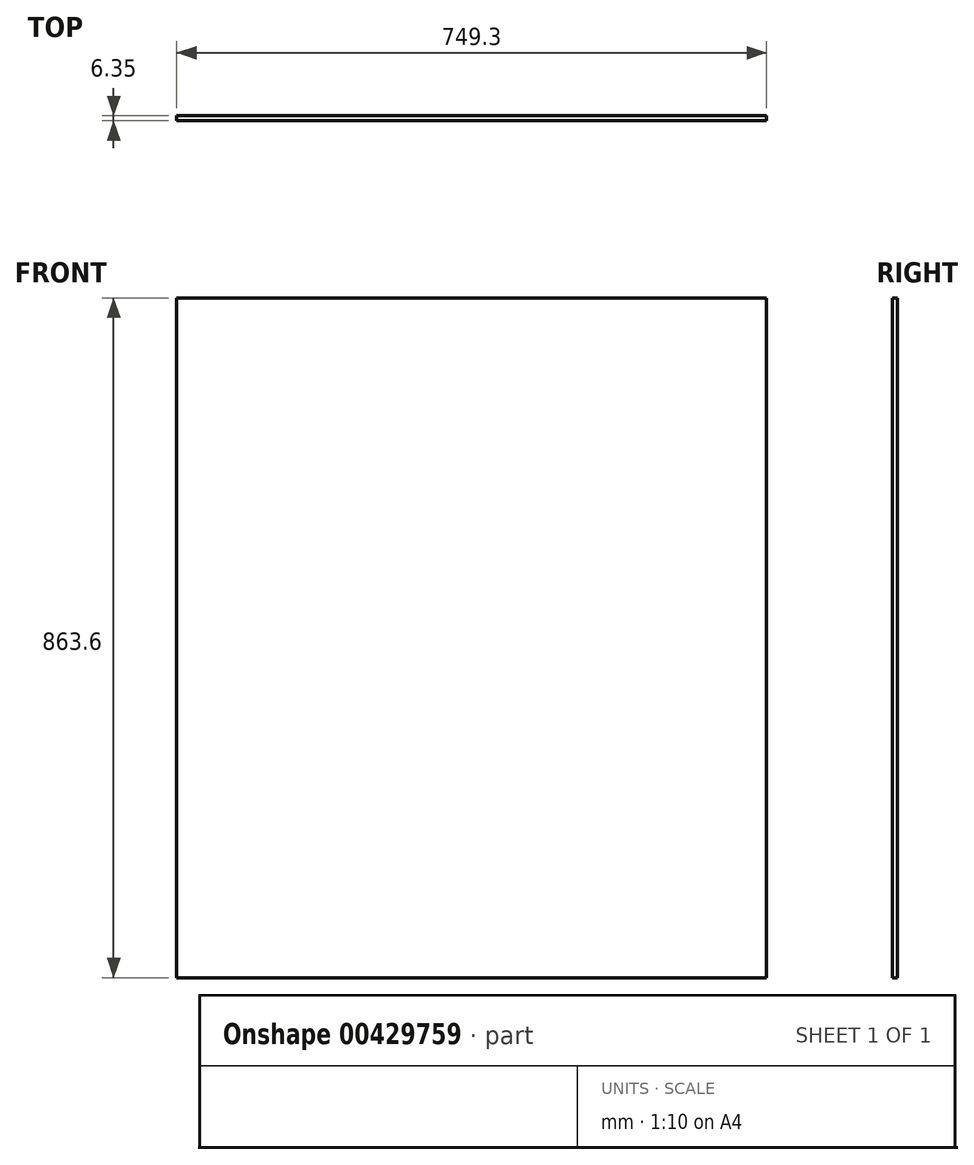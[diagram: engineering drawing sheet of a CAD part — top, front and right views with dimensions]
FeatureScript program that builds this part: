
annotation { "Feature Type Name" : "Feature", "Feature Type Description" : "" }
export const myFeature = defineFeature(function(context is Context, id is Id, definition is map)
    precondition{}
    {
        {
            var Q0;
            Q0=qCreatedBy(makeId("Front.planeOp"),FACE);
            var sketch = newSketch(context, id + "F0", { "sketchPlane" : qUnion([Q0])});
            skLineSegment(sketch, "E0.bottom", {"start": v(0, 0) * mm, "end": v(749.3, 0) * mm});
            skLineSegment(sketch, "E0.top", {"start": v(0, 863.6) * mm, "end": v(749.3, 863.6) * mm});
            skLineSegment(sketch, "E0.left", {"start": v(0, 0) * mm, "end": v(0, 863.6) * mm});
            skLineSegment(sketch, "E0.right", {"start": v(749.3, 0) * mm, "end": v(749.3, 863.6) * mm});
            skSolve(sketch);
        }
        {
            var Q0;
            Q0 = qSketchRegion(id + "F0", true);
            extrude(context, id + "F1", {"entities" : qUnion([Q0]), "depth" : 6.35 * mm});
        }
    });
